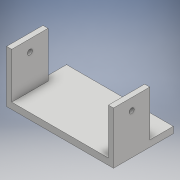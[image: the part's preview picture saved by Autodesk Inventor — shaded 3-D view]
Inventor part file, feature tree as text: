
AUTODESK INVENTOR PART (.ipt)
format: ipt  version: 2018.1 (Build 221171000, 171)  size: 173,056 bytes
history: native  units: mm
features: extrude x6, sketch x6, projected_geometry x5, other x1
ambient origin geometry x8: Origin, YZ Plane, XZ Plane, XY Plane, X Axis, Y Axis, Z Axis, Center Point
bodies: Body1 (feature_tree)
feature tree (18):
  other  "Твердое тело1"
  extrude  "Выдавливание1"  Depth=76.0mm
  extrude  "Выдавливание2"  Depth=104.76mm
  extrude  "Выдавливание3"  Depth=53.241mm
  extrude  "Выдавливание4"  Depth=66.1mm
  extrude  "Выдавливание5"  Depth=5.0mm
  extrude  "Выдавливание6"  Depth=5.0mm
  sketch  "Эскиз1"
  sketch  "Эскиз2"
  sketch  "Эскиз3"
  projected_geometry  "Спроецированная петля1"
  sketch  "Эскиз4"
  projected_geometry  "Спроецированная петля2"
  sketch  "Эскиз5"
  projected_geometry  "Спроецированная петля3"
  projected_geometry  "Спроецированная петля4"
  sketch  "Эскиз6"
  projected_geometry  "Спроецированная петля5"
